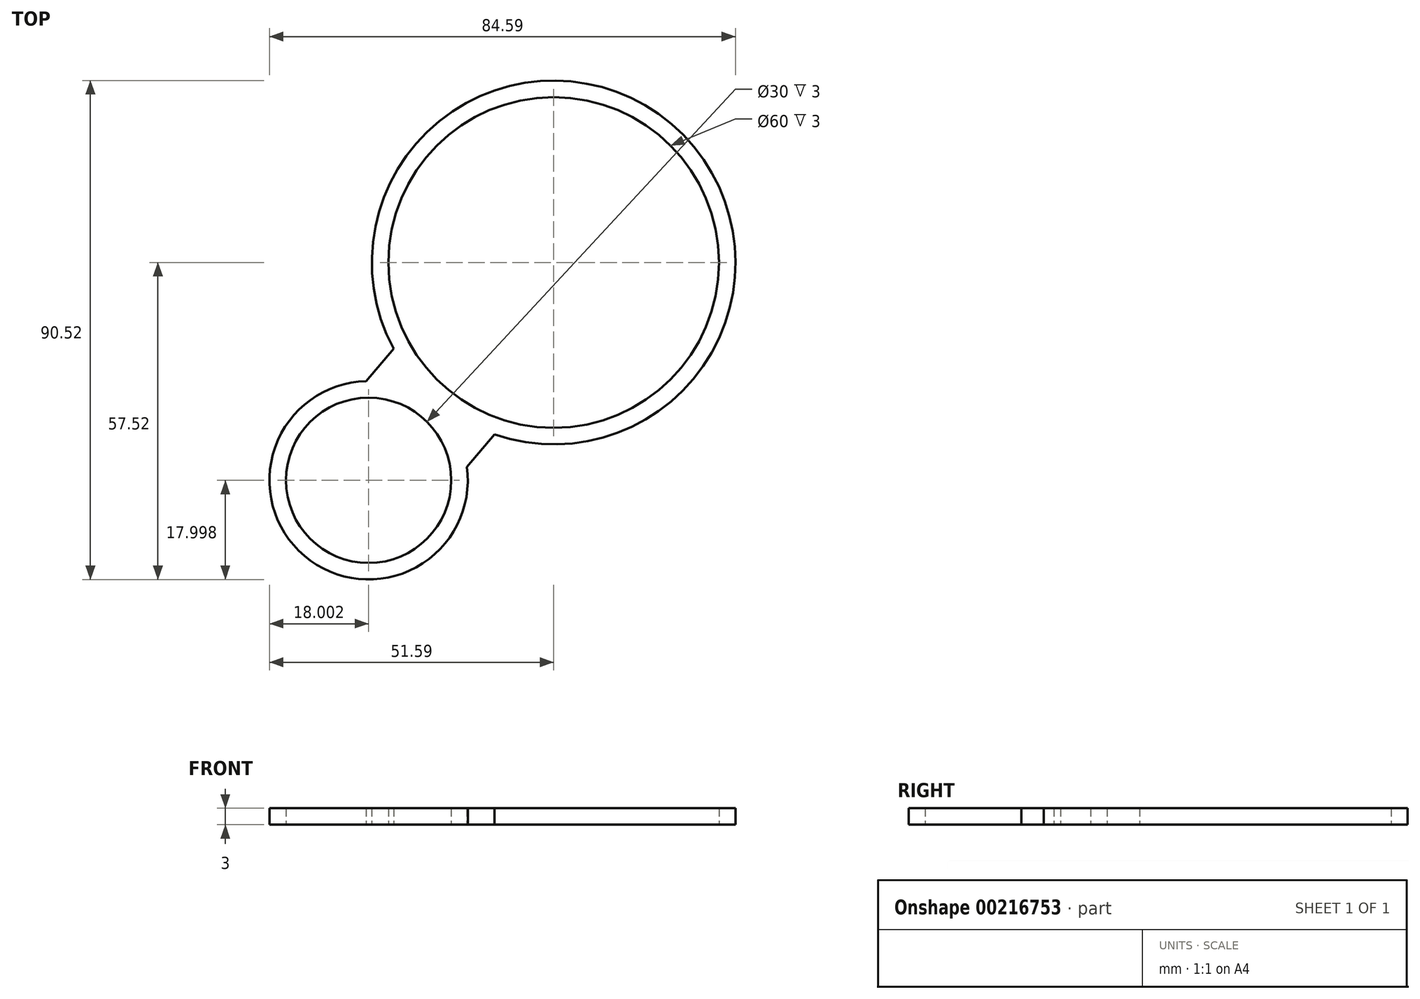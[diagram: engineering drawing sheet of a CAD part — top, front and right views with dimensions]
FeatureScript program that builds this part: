
annotation { "Feature Type Name" : "Feature", "Feature Type Description" : "" }
export const myFeature = defineFeature(function(context is Context, id is Id, definition is map)
    precondition{}
    {
        {
            var Q0;
            Q0=qCreatedBy(makeId("Top.planeOp"),FACE);
            var sketch = newSketch(context, id + "F0", { "sketchPlane" : qUnion([Q0])});
            skCircle(sketch, "E0", {"center": v(0, 0) * mm, "radius": 30 * mm});
            skCircle(sketch, "E1", {"center": v(0, 0) * mm, "radius": 33 * mm});
            skCircle(sketch, "E2", {"center": v(-33.59, -39.52) * mm, "radius": 15 * mm});
            skCircle(sketch, "E3", {"center": v(-33.59, -39.52) * mm, "radius": 18 * mm});
            skLineSegment(sketch, "E4", {"start": v(-34.04, -21.53) * mm, "end": v(-29.05, -15.65) * mm});
            skLineSegment(sketch, "E5", {"start": v(-15.76, -37.07) * mm, "end": v(-10.76, -31.2) * mm});
            skLineSegment(sketch, "E6", {"start": v(-33.59, -39.52) * mm, "end": v(0, 0) * mm});
            skSolve(sketch);
        }
        {
            var Q0;
            Q0=makeQuery(id+"F0.imprint","IMPRINT",FACE,{"disambiguationData":[TD([[makeQuery(id+"F0.imprint","IMPRINT",EDGE,{"derivedFrom":sQuery(id+"F0.wireOp",EDGE,"E2")}),-1.0]])]});
            var Q1;
            Q1=makeQuery(id+"F0.imprint","IMPRINT",FACE,{"disambiguationData":[TD([[makeQuery(id+"F0.imprint","IMPRINT",EDGE,{"derivedFrom":sQuery(id+"F0.wireOp",EDGE,"E0")}),-1.0]])]});
            var Q2;
            {var subQ0=sQuery(id+"F0.wireOp",EDGE,"E5");Q2=makeQuery(id+"F0.imprint","IMPRINT",FACE,{"disambiguationData":[TD([[makeQuery(id+"F0.imprint","IMPRINT",EDGE,{"derivedFrom":subQ0}),1.0]])]});}
            var Q3;
            {var subQ0=sQuery(id+"F0.wireOp",EDGE,"E4");Q3=makeQuery(id+"F0.imprint","IMPRINT",FACE,{"disambiguationData":[TD([[makeQuery(id+"F0.imprint","IMPRINT",EDGE,{"derivedFrom":subQ0}),-1.0]])]});}
            extrude(context, id + "F1", {"entities" : qUnion([Q0, Q1, Q2, Q3]), "depth" : 3 * mm});
        }
    });
